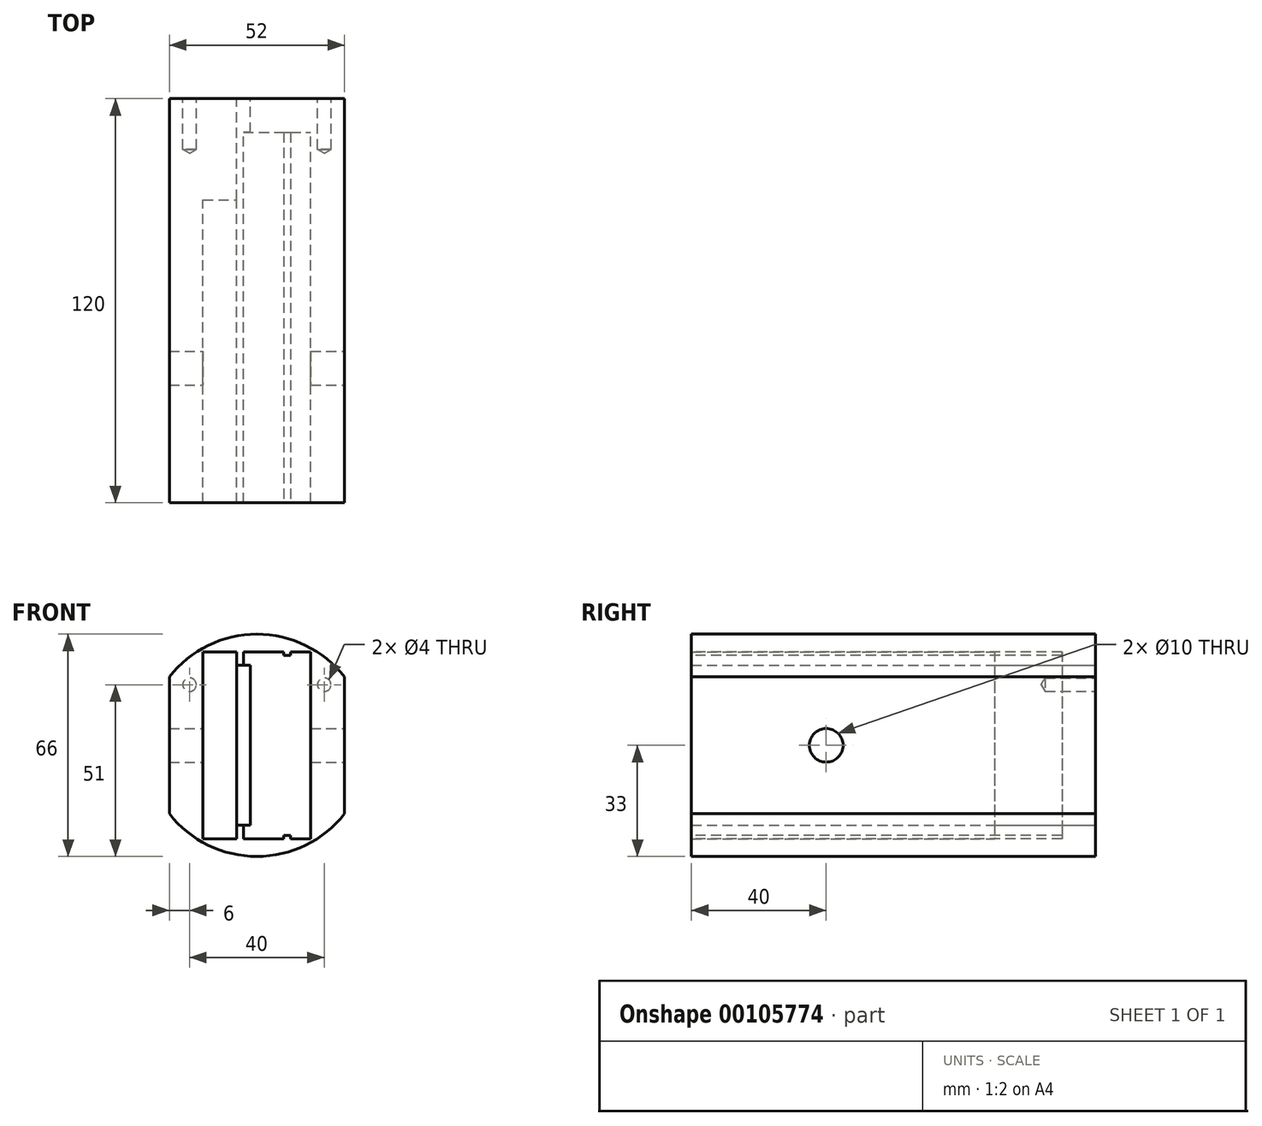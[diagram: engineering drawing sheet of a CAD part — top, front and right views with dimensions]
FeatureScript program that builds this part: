
annotation { "Feature Type Name" : "Feature", "Feature Type Description" : "" }
export const myFeature = defineFeature(function(context is Context, id is Id, definition is map)
    precondition{}
    {
        {
            var Q0;
            Q0=qCreatedBy(makeId("Front.planeOp"),FACE);
            var sketch = newSketch(context, id + "F0", { "sketchPlane" : qUnion([Q0])});
            skCircle(sketch, "E0", {"center": v(0, 0) * mm, "radius": 33 * mm});
            skLineSegment(sketch, "E1.bottom", {"start": v(-16, 27.75) * mm, "end": v(-6, 27.75) * mm});
            skLineSegment(sketch, "E1.top", {"start": v(-16, -27.75) * mm, "end": v(-6, -27.75) * mm});
            skLineSegment(sketch, "E1.left", {"start": v(-16, 27.75) * mm, "end": v(-16, -27.75) * mm});
            skLineSegment(sketch, "E1.right", {"start": v(-6, 27.75) * mm, "end": v(-6, -27.75) * mm});
            skPoint(sketch, "E1.middle", {"position": v(-11, 0) * mm});
            skLineSegment(sketch, "E2.bottom", {"start": v(-4, 27.75) * mm, "end": v(16, 27.75) * mm});
            skLineSegment(sketch, "E2.top", {"start": v(-4, -27.75) * mm, "end": v(16, -27.75) * mm});
            skLineSegment(sketch, "E2.left", {"start": v(-4, 27.75) * mm, "end": v(-4, -27.75) * mm});
            skLineSegment(sketch, "E2.right", {"start": v(16, 27.75) * mm, "end": v(16, -27.75) * mm});
            skPoint(sketch, "E2.middle", {"position": v(6, 0) * mm});
            skLineSegment(sketch, "E3", {"start": v(-26, -20.32) * mm, "end": v(-26, 20.32) * mm});
            skLineSegment(sketch, "E4", {"start": v(26, 20.32) * mm, "end": v(26, -20.32) * mm});
            skLineSegment(sketch, "E5", {"start": v(-6, 23.75) * mm, "end": v(-4, 23.75) * mm});
            skLineSegment(sketch, "E6", {"start": v(-6, -23.75) * mm, "end": v(-4, -23.75) * mm});
            skPoint(sketch, "E7", {"position": v(20, 18) * mm});
            skPoint(sketch, "E8", {"position": v(-20, 18) * mm});
            skSolve(sketch);
        }
        {
            var Q0;
            Q0=makeQuery(id+"F0.imprint","IMPRINT",FACE,{"disambiguationData":[TD([[makeQuery(id+"F0.imprint","IMPRINT",EDGE,{"derivedFrom":sQuery(id+"F0.wireOp",EDGE,"E1.bottom")}),1.0]])]});
            extrude(context, id + "F1", {"entities" : qUnion([Q0]), "depth" : 120 * mm});
        }
        {
            var Q0;
            Q0=makeQuery(id+"F0.imprint","IMPRINT",FACE,{"disambiguationData":[TD([[makeQuery(id+"F0.imprint","IMPRINT",EDGE,{"derivedFrom":sQuery(id+"F0.wireOp",EDGE,"E2.bottom")}),-1.0]])]});
            extrude(context, id + "F2", {"entities" : qUnion([Q0]), "operationType" : NewBodyOperationType.ADD, "depth" : 10 * mm});
        }
        {
            var Q0;
            Q0=makeQuery(id+"F0.imprint","IMPRINT",FACE,{"disambiguationData":[TD([[makeQuery(id+"F0.imprint","IMPRINT",EDGE,{"derivedFrom":sQuery(id+"F0.wireOp",EDGE,"E1.bottom")}),-1.0]])]});
            extrude(context, id + "F3", {"entities" : qUnion([Q0]), "operationType" : NewBodyOperationType.ADD, "depth" : 45 * mm});
        }
        {
            var Q0;
            Q0=sQuery(id+"F0.wireOp",VERTEX,"E7");
            var Q1;
            Q1=sQuery(id+"F0.wireOp",VERTEX,"E8");
            var Q2;
            Q2=makeQuery(id+"F1.opExtrude","SWEPT_BODY",BODY,{"disambiguationData":[OSD([sQuery(id+"F0.wireOp",EDGE,"E0"),sQuery(id+"F0.wireOp",EDGE,"E1.bottom"),sQuery(id+"F0.wireOp",EDGE,"E1.top"),sQuery(id+"F0.wireOp",EDGE,"E1.left"),sQuery(id+"F0.wireOp",EDGE,"E1.right"),sQuery(id+"F0.wireOp",EDGE,"E2.bottom"),sQuery(id+"F0.wireOp",EDGE,"E2.top"),sQuery(id+"F0.wireOp",EDGE,"E2.left"),sQuery(id+"F0.wireOp",EDGE,"E2.right"),sQuery(id+"F0.wireOp",EDGE,"E3"),sQuery(id+"F0.wireOp",EDGE,"E4"),sQuery(id+"F0.wireOp",EDGE,"E5"),sQuery(id+"F0.wireOp",EDGE,"E6")])]});
            hole(context, id + "F4", {"style" : HoleStyle.SIMPLE, "endStyle" : HoleEndStyle.BLIND, "oppositeDirection" : true, "holeDiameter" : 4 * mm, "holeDepth" : 15 * mm, "tappedDepth" : 12 * mm, "tapClearance" : 3, "locations" : qUnion([Q0, Q1]), "scope" : qUnion([Q2])});
        }
        {
            var Q0;
            Q0=makeQuery(id+"F1.opExtrude","SWEPT_FACE",FACE,{"disambiguationData":[OSD([sQuery(id+"F0.wireOp",EDGE,"E4")])]});
            var sketch = newSketch(context, id + "F5", { "sketchPlane" : qUnion([Q0])});
            skPoint(sketch, "E9", {"position": v(-80, 0) * mm});
            skPoint(sketch, "E9.positionSnap0", {"position": v(-120, 0) * mm});
            skSolve(sketch);
        }
        {
            var Q0;
            Q0=sQuery(id+"F5.wireOp",VERTEX,"E9");
            var Q1;
            Q1=makeQuery(id+"F1.opExtrude","SWEPT_BODY",BODY,{"disambiguationData":[OSD([sQuery(id+"F0.wireOp",EDGE,"E0"),sQuery(id+"F0.wireOp",EDGE,"E1.bottom"),sQuery(id+"F0.wireOp",EDGE,"E1.top"),sQuery(id+"F0.wireOp",EDGE,"E1.left"),sQuery(id+"F0.wireOp",EDGE,"E1.right"),sQuery(id+"F0.wireOp",EDGE,"E2.bottom"),sQuery(id+"F0.wireOp",EDGE,"E2.top"),sQuery(id+"F0.wireOp",EDGE,"E2.left"),sQuery(id+"F0.wireOp",EDGE,"E2.right"),sQuery(id+"F0.wireOp",EDGE,"E3"),sQuery(id+"F0.wireOp",EDGE,"E4"),sQuery(id+"F0.wireOp",EDGE,"E5"),sQuery(id+"F0.wireOp",EDGE,"E6")])]});
            hole(context, id + "F6", {"style" : HoleStyle.SIMPLE, "endStyle" : HoleEndStyle.THROUGH, "holeDiameter" : 10 * mm, "tappedDepth" : 12 * mm, "tapClearance" : 3, "locations" : qUnion([Q0]), "scope" : qUnion([Q1])});
        }
        {
            var Q0;
            Q0=makeQuery(id+"F3.opExtrude","CAP_FACE",FACE,{"disambiguationData":[OSD([sQuery(id+"F0.wireOp",EDGE,"E1.bottom"),sQuery(id+"F0.wireOp",EDGE,"E1.top"),sQuery(id+"F0.wireOp",EDGE,"E1.left"),sQuery(id+"F0.wireOp",EDGE,"E1.right")])],"isStart":false});
            extrude(context, id + "F7", {"entities" : qUnion([Q0]), "operationType" : NewBodyOperationType.REMOVE, "oppositeDirection" : true, "depth" : 15 * mm});
        }
        {
            var Q0;
            Q0=makeQuery(id+"F1.opExtrude","CAP_FACE",FACE,{"disambiguationData":[OSD([sQuery(id+"F0.wireOp",EDGE,"E0"),sQuery(id+"F0.wireOp",EDGE,"E1.bottom"),sQuery(id+"F0.wireOp",EDGE,"E1.top"),sQuery(id+"F0.wireOp",EDGE,"E1.left"),sQuery(id+"F0.wireOp",EDGE,"E1.right"),sQuery(id+"F0.wireOp",EDGE,"E2.bottom"),sQuery(id+"F0.wireOp",EDGE,"E2.top"),sQuery(id+"F0.wireOp",EDGE,"E2.left"),sQuery(id+"F0.wireOp",EDGE,"E2.right"),sQuery(id+"F0.wireOp",EDGE,"E3"),sQuery(id+"F0.wireOp",EDGE,"E4"),sQuery(id+"F0.wireOp",EDGE,"E5"),sQuery(id+"F0.wireOp",EDGE,"E6")])],"isStart":false});
            var sketch = newSketch(context, id + "F8", { "sketchPlane" : qUnion([Q0])});
            skLineSegment(sketch, "E10.bottom", {"start": v(10, 27.75) * mm, "end": v(8, 27.75) * mm});
            skLineSegment(sketch, "E10.top", {"start": v(10, 26.75) * mm, "end": v(8, 26.75) * mm});
            skLineSegment(sketch, "E10.left", {"start": v(10, 27.75) * mm, "end": v(10, 26.75) * mm});
            skLineSegment(sketch, "E10.right", {"start": v(8, 27.75) * mm, "end": v(8, 26.75) * mm});
            skLineSegment(sketch, "E11.MirrorCS", {"start": v(8, -27.75) * mm, "end": v(8, -26.75) * mm});
            skLineSegment(sketch, "E12.MirrorCS", {"start": v(10, -26.75) * mm, "end": v(8, -26.75) * mm});
            skLineSegment(sketch, "E13.MirrorCS", {"start": v(10, -27.75) * mm, "end": v(10, -26.75) * mm});
            skSolve(sketch);
        }
        {
            var Q0;
            Q0=makeQuery(id+"F8.imprint","IMPRINT",FACE,{"disambiguationData":[TD([[makeQuery(id+"F8.imprint","IMPRINT",EDGE,{"derivedFrom":sQuery(id+"F8.wireOp",EDGE,"E10.bottom")}),-1.0]])]});
            var Q1;
            {var subQ0=sQuery(id+"F8.wireOp",EDGE,"E11.MirrorCS");Q1=makeQuery(id+"F8.imprint","IMPRINT",FACE,{"disambiguationData":[TD([[makeQuery(id+"F8.imprint","IMPRINT",EDGE,{"derivedFrom":subQ0}),-1.0]])]});}
            extrude(context, id + "F9", {"entities" : qUnion([Q0, Q1]), "operationType" : NewBodyOperationType.ADD, "endBound" : BoundingType.UP_TO_NEXT, "oppositeDirection" : true, "depth" : 25 * mm});
        }
        {
            var Q0;
            Q0=makeQuery(id+"F2.opExtrude","SWEPT_FACE",FACE,{"disambiguationData":[OSD([sQuery(id+"F0.wireOp",EDGE,"E2.left")])]});
            extrude(context, id + "F10", {"entities" : qUnion([Q0]), "operationType" : NewBodyOperationType.REMOVE, "oppositeDirection" : true, "depth" : 2 * mm});
        }
    });
